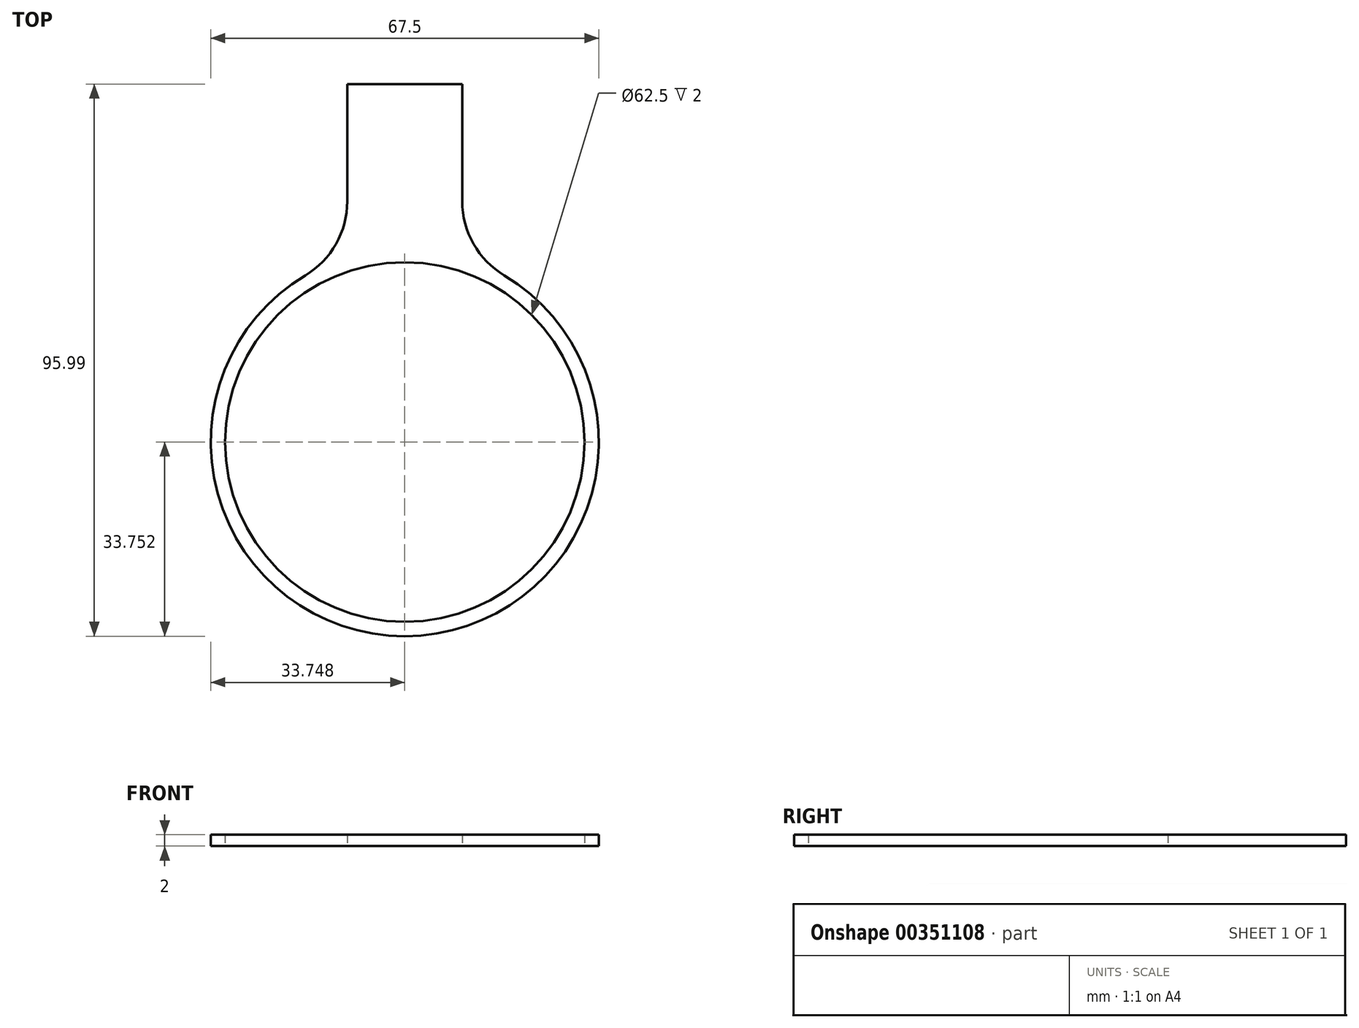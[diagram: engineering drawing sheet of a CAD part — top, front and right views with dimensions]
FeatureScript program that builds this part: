
annotation { "Feature Type Name" : "Feature", "Feature Type Description" : "" }
export const myFeature = defineFeature(function(context is Context, id is Id, definition is map)
    precondition{}
    {
        {
            var Q0;
            Q0=qCreatedBy(makeId("Top.planeOp"),FACE);
            var sketch = newSketch(context, id + "F0", { "sketchPlane" : qUnion([Q0])});
            skCircle(sketch, "E0", {"center": v(-1.07, -59.33) * mm, "radius": 31.25 * mm});
            skArc(sketch, "E1", {"start": v(-18.38, -30.35) * mm, "mid": v(-1.07, -93.08) * mm, "end": v(16.24, -30.35) * mm});
            skLineSegment(sketch, "E2.bottom", {"start": v(-11.07, 2.9) * mm, "end": v(8.93, 2.9) * mm});
            skLineSegment(sketch, "E2.left", {"start": v(-11.07, 2.9) * mm, "end": v(-11.07, -17.48) * mm});
            skLineSegment(sketch, "E2.right", {"start": v(8.93, 2.9) * mm, "end": v(8.93, -17.48) * mm});
            skPoint(sketch, "E3.visualSharp", {"position": v(-11.07, -27.1) * mm});
            skArc(sketch, "E3.filletArc", {"start": v(-18.38, -30.35) * mm, "mid": v(-13.03, -24.88) * mm, "end": v(-11.07, -17.48) * mm});
            skPoint(sketch, "E4.visualSharp", {"position": v(8.93, -27.1) * mm});
            skArc(sketch, "E4.filletArc", {"start": v(8.93, -17.48) * mm, "mid": v(10.88, -24.88) * mm, "end": v(16.24, -30.35) * mm});
            skPoint(sketch, "E5.visualSharp", {"position": v(-11.07, 22.9) * mm});
            skPoint(sketch, "E6.visualSharp", {"position": v(8.93, 22.9) * mm});
            skPoint(sketch, "E7", {"position": v(-1.07, 12.9) * mm});
            skLineSegment(sketch, "E8.top", {"start": v(-6.07, 22.9) * mm, "end": v(3.93, 22.9) * mm});
            skLineSegment(sketch, "E8.left", {"start": v(-11.07, 2.9) * mm, "end": v(-11.07, 17.9) * mm});
            skLineSegment(sketch, "E8.right", {"start": v(8.93, 2.9) * mm, "end": v(8.93, 17.9) * mm});
            skArc(sketch, "E9.filletArc", {"start": v(-6.07, 22.9) * mm, "mid": v(-9.6, 21.44) * mm, "end": v(-11.07, 17.9) * mm});
            skArc(sketch, "E10.filletArc", {"start": v(8.93, 17.9) * mm, "mid": v(7.46, 21.44) * mm, "end": v(3.93, 22.9) * mm});
            skLineSegment(sketch, "E11", {"start": v(-6.07, 17.9) * mm, "end": v(8.93, 2.9) * mm, "construction": true});
            skLineSegment(sketch, "E12", {"start": v(3.93, 17.9) * mm, "end": v(-11.07, 2.9) * mm, "construction": true});
            skCircle(sketch, "E13", {"center": v(-1.07, 12.9) * mm, "radius": 4 * mm});
            skSolve(sketch);
        }
        {
            var Q0;
            Q0=makeQuery(id+"F0.imprint","IMPRINT",FACE,{"disambiguationData":[TD([[makeQuery(id+"F0.imprint","IMPRINT",EDGE,{"derivedFrom":sQuery(id+"F0.wireOp",EDGE,"E2.bottom")}),1.0]])]});
            var Q1;
            Q1=makeQuery(id+"F0.imprint","IMPRINT",FACE,{"disambiguationData":[TD([[makeQuery(id+"F0.imprint","IMPRINT",EDGE,{"derivedFrom":sQuery(id+"F0.wireOp",EDGE,"E0")}),-1.0]])]});
            extrude(context, id + "F1", {"entities" : qUnion([Q0, Q1]), "depth" : 2 * mm});
        }
    });
